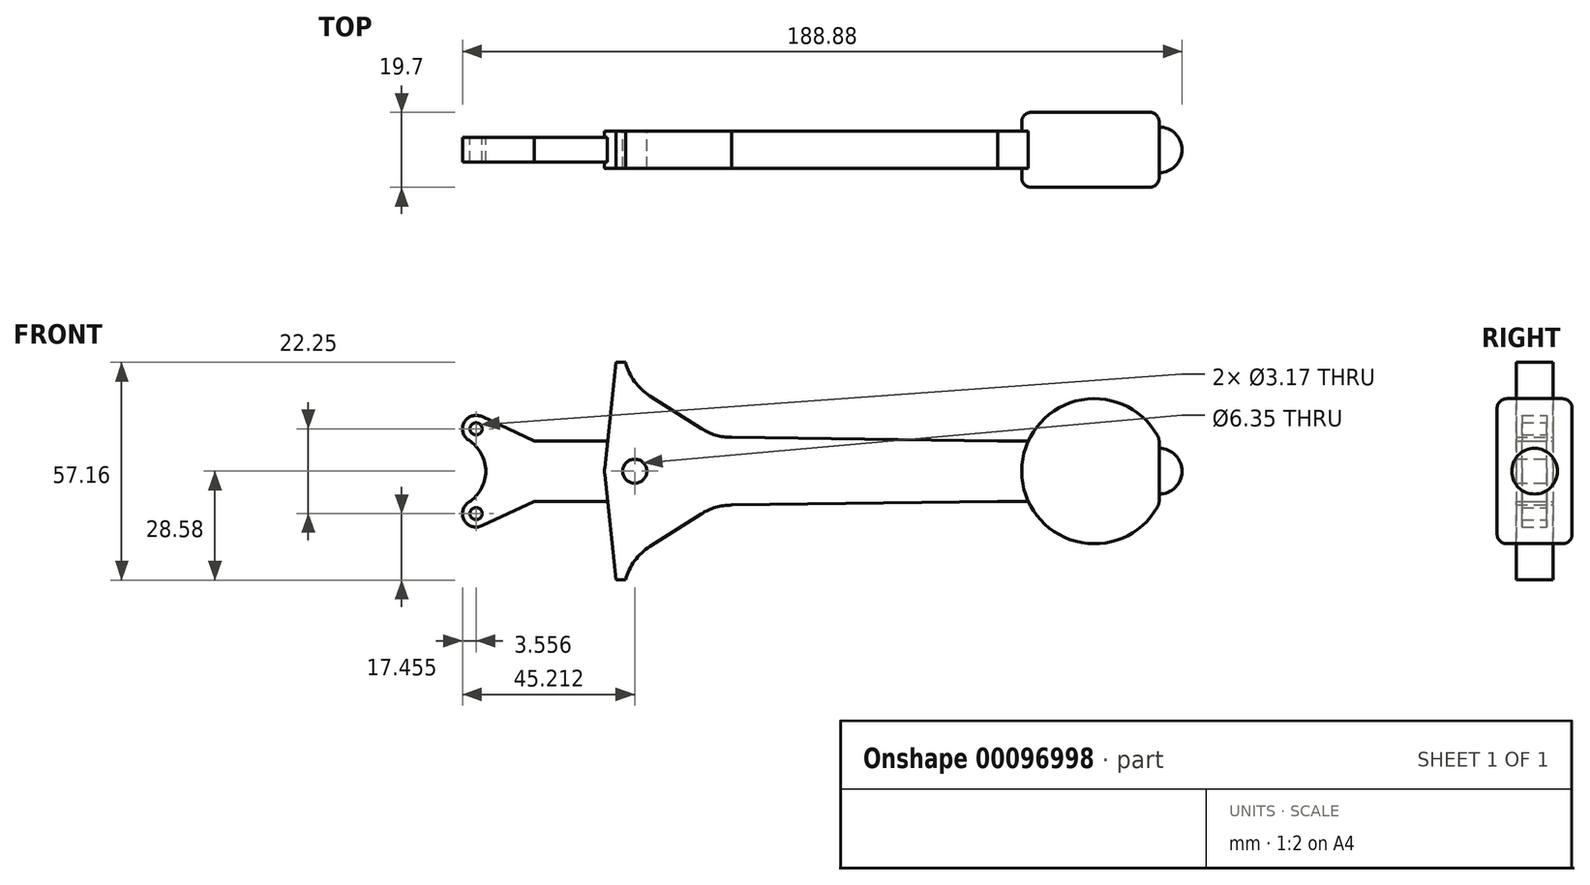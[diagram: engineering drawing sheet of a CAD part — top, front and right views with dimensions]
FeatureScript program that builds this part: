
annotation { "Feature Type Name" : "Feature", "Feature Type Description" : "" }
export const myFeature = defineFeature(function(context is Context, id is Id, definition is map)
    precondition{}
    {
        {
            var Q0;
            Q0=qCreatedBy(makeId("Front.planeOp"),FACE);
            var sketch = newSketch(context, id + "F0", { "sketchPlane" : qUnion([Q0])});
            skArc(sketch, "E0", {"start": v(-89.8, -8.13) * mm, "mid": v(-85.35, 0) * mm, "end": v(-89.8, 8.13) * mm});
            skLineSegment(sketch, "E1", {"start": v(-86.38, -14.35) * mm, "end": v(-72.63, -7.94) * mm});
            skLineSegment(sketch, "E2", {"start": v(-86.38, 14.35) * mm, "end": v(-72.63, 7.94) * mm});
            skArc(sketch, "E3", {"start": v(-86.38, 14.35) * mm, "mid": v(-91, 12.84) * mm, "end": v(-89.8, 8.13) * mm});
            skArc(sketch, "E4", {"start": v(-89.8, -8.13) * mm, "mid": v(-91, -12.84) * mm, "end": v(-86.38, -14.35) * mm});
            skLineSegment(sketch, "E5", {"start": v(-72.63, -7.94) * mm, "end": v(-53.37, -7.94) * mm});
            skLineSegment(sketch, "E6", {"start": v(-72.63, 7.94) * mm, "end": v(-53.37, 7.94) * mm});
            skCircle(sketch, "E7", {"center": v(-87.88, -11.13) * mm, "radius": 1.59 * mm});
            skCircle(sketch, "E8", {"center": v(-87.88, 11.13) * mm, "radius": 1.59 * mm});
            skLineSegment(sketch, "E9", {"start": v(-42.24, 19.76) * mm, "end": v(-28.77, 11.2) * mm});
            skArc(sketch, "E10", {"start": v(-28.77, 11.2) * mm, "mid": v(-24.97, 9.48) * mm, "end": v(-20.83, 8.89) * mm});
            skLineSegment(sketch, "E11", {"start": v(-48.63, 28.57) * mm, "end": v(-51.17, 28.58) * mm});
            skArc(sketch, "E12", {"start": v(-48.63, 28.57) * mm, "mid": v(-46.27, 23.56) * mm, "end": v(-42.24, 19.76) * mm});
            skArc(sketch, "E13", {"start": v(-54.12, 0.84) * mm, "mid": v(-54.15, 0.42) * mm, "end": v(-54.17, 0) * mm});
            skLineSegment(sketch, "E14", {"start": v(-54.12, 0.84) * mm, "end": v(-51.17, 28.58) * mm});
            skCircle(sketch, "E15", {"center": v(-46.23, 0) * mm, "radius": 3.17 * mm});
            skArc(sketch, "E16", {"start": v(-20.83, -8.9) * mm, "mid": v(-24.97, -9.48) * mm, "end": v(-28.77, -11.2) * mm});
            skLineSegment(sketch, "E17", {"start": v(-54.12, -0.84) * mm, "end": v(-51.17, -28.57) * mm});
            skLineSegment(sketch, "E18", {"start": v(-42.24, -19.76) * mm, "end": v(-28.77, -11.2) * mm});
            skArc(sketch, "E19", {"start": v(-42.24, -19.76) * mm, "mid": v(-46.27, -23.56) * mm, "end": v(-48.63, -28.58) * mm});
            skLineSegment(sketch, "E20", {"start": v(-48.63, -28.58) * mm, "end": v(-51.17, -28.57) * mm});
            skLineSegment(sketch, "E21", {"start": v(-20.83, -8.9) * mm, "end": v(49.02, -7.94) * mm});
            skLineSegment(sketch, "E22", {"start": v(-20.83, 8.89) * mm, "end": v(49.02, 7.94) * mm});
            skLineSegment(sketch, "E23", {"start": v(49.02, -7.94) * mm, "end": v(57.1, -7.94) * mm});
            skLineSegment(sketch, "E24", {"start": v(49.02, 7.94) * mm, "end": v(57.1, 7.94) * mm});
            skArc(sketch, "E25", {"start": v(57.1, -7.94) * mm, "mid": v(74.08, -19.05) * mm, "end": v(91.44, -8.56) * mm});
            skArc(sketch, "E26", {"start": v(91.44, 8.56) * mm, "mid": v(74.08, 19.05) * mm, "end": v(57.1, 7.94) * mm});
            skArc(sketch, "E27", {"start": v(-54.17, 0) * mm, "mid": v(-54.15, -0.42) * mm, "end": v(-54.12, -0.84) * mm});
            skLineSegment(sketch, "E28", {"start": v(91.44, 8.56) * mm, "end": v(91.44, -8.56) * mm});
            skSolve(sketch);
        }
        {
            var Q0;
            Q0=makeQuery(id+"F0.imprint","IMPRINT",FACE,{"disambiguationData":[TD([[makeQuery(id+"F0.imprint","IMPRINT",EDGE,{"derivedFrom":sQuery(id+"F0.wireOp",EDGE,"E9")}),-1.0]])]});
            extrude(context, id + "F1", {"entities" : qUnion([Q0]), "endBound" : BoundingType.SYMMETRIC, "depth" : 9.7 * mm});
        }
        {
            var Q0;
            Q0=qCreatedBy(makeId("Front.planeOp"),FACE);
            var sketch = newSketch(context, id + "F2", { "sketchPlane" : qUnion([Q0])});
            skArc(sketch, "E29.0", {"start": v(91.44, 8.56) * mm, "mid": v(74.08, 19.05) * mm, "end": v(57.1, 7.94) * mm});
            skArc(sketch, "E30.0", {"start": v(57.1, 7.94) * mm, "mid": v(66.17, -17.17) * mm, "end": v(91.44, -8.56) * mm});
            skLineSegment(sketch, "E31", {"start": v(91.44, 8.56) * mm, "end": v(91.44, -8.56) * mm});
            skPoint(sketch, "E32.orphan", {"position": v(57.1, -7.94) * mm});
            skSolve(sketch);
        }
        {
            var Q0;
            Q0 = qSketchRegion(id + "F2", true);
            extrude(context, id + "F3", {"entities" : qUnion([Q0]), "operationType" : NewBodyOperationType.ADD, "endBound" : BoundingType.SYMMETRIC, "depth" : 19.7 * mm});
        }
        {
            var Q0;
            Q0=makeQuery(id+"F0.imprint","IMPRINT",FACE,{"disambiguationData":[TD([[makeQuery(id+"F0.imprint","IMPRINT",EDGE,{"derivedFrom":sQuery(id+"F0.wireOp",EDGE,"E0")}),-1.0]])]});
            extrude(context, id + "F4", {"entities" : qUnion([Q0]), "operationType" : NewBodyOperationType.ADD, "endBound" : BoundingType.SYMMETRIC, "depth" : 6.5 * mm});
        }
        {
            var Q0;
            Q0=qCreatedBy(makeId("Front.planeOp"),FACE);
            var sketch = newSketch(context, id + "F5", { "sketchPlane" : qUnion([Q0])});
            skArc(sketch, "E33", {"start": v(97.44, 0) * mm, "mid": v(95.68, 4.24) * mm, "end": v(91.44, 6) * mm});
            skLineSegment(sketch, "E34", {"start": v(74.08, 0) * mm, "end": v(74.13, 0) * mm, "construction": true});
            skLineSegment(sketch, "E35", {"start": v(91.44, 6) * mm, "end": v(90.44, 6) * mm});
            skLineSegment(sketch, "E36", {"start": v(90.44, 6) * mm, "end": v(90.44, 0) * mm});
            skPoint(sketch, "E37.start.orphan", {"position": v(90.44, -4.99) * mm});
            skLineSegment(sketch, "E38", {"start": v(74.13, 0) * mm, "end": v(101.12, 0) * mm, "construction": true});
            skLineSegment(sketch, "E39", {"start": v(90.44, 0) * mm, "end": v(97.44, 0) * mm});
            skSolve(sketch);
        }
        {
            var Q0;
            Q0=makeQuery(id+"F5.imprint","IMPRINT",FACE,{"disambiguationData":[TD([[makeQuery(id+"F5.imprint","IMPRINT",EDGE,{"derivedFrom":sQuery(id+"F5.wireOp",EDGE,"E33")}),1.0]])]});
            var Q1;
            Q1=sQuery(id+"F5.wireOp",EDGE,"E38");
            revolve(context, id + "F6", {"operationType" : NewBodyOperationType.ADD, "entities" : qUnion([Q0]), "axis" : qUnion([Q1]), "revolveType" : RevolveType.FULL});
        }
        {
            var Q0;
            Q0=makeQuery(id+"F3.boolean.opBoolean","MERGE",EDGE,{"derivedFrom":[makeQuery(id+"F1.opExtrude","SWEPT_EDGE",EDGE,{"disambiguationData":[OSD([sQuery(id+"F0.wireOp",EDGE,"E25"),sQuery(id+"F0.wireOp",EDGE,"E28")])]}),makeQuery(id+"F3.opExtrude","SWEPT_EDGE",EDGE,{"disambiguationData":[OSD([sQuery(id+"F2.wireOp",EDGE,"E30.0"),sQuery(id+"F2.wireOp",EDGE,"E31")])]})]});
            var Q1;
            Q1=makeQuery(id+"F3.boolean.opBoolean","MERGE",EDGE,{"derivedFrom":[makeQuery(id+"F1.opExtrude","SWEPT_EDGE",EDGE,{"disambiguationData":[OSD([sQuery(id+"F0.wireOp",EDGE,"E26"),sQuery(id+"F0.wireOp",EDGE,"E28")])]}),makeQuery(id+"F3.opExtrude","SWEPT_EDGE",EDGE,{"disambiguationData":[OSD([sQuery(id+"F2.wireOp",EDGE,"E29.0"),sQuery(id+"F2.wireOp",EDGE,"E31")])]})]});
            fillet(context, id + "F7", {"entities" : qUnion([Q0, Q1]), "radius" : 3.5 * mm, "tangentPropagation" : true, "allowEdgeOverflow" : false});
        }
        {
            var Q0;
            Q0=makeQuery(id+"F3.opExtrude","CAP_FACE",FACE,{"disambiguationData":[OSD([sQuery(id+"F2.wireOp",EDGE,"E29.0"),sQuery(id+"F2.wireOp",EDGE,"E30.0"),sQuery(id+"F2.wireOp",EDGE,"E31")])],"isStart":false});
            var Q1;
            Q1=makeQuery(id+"F3.opExtrude","CAP_FACE",FACE,{"disambiguationData":[OSD([sQuery(id+"F2.wireOp",EDGE,"E29.0"),sQuery(id+"F2.wireOp",EDGE,"E30.0"),sQuery(id+"F2.wireOp",EDGE,"E31")])],"isStart":true});
            fillet(context, id + "F8", {"entities" : qUnion([Q0, Q1]), "radius" : 2.5 * mm, "tangentPropagation" : true, "allowEdgeOverflow" : false});
        }
    });
